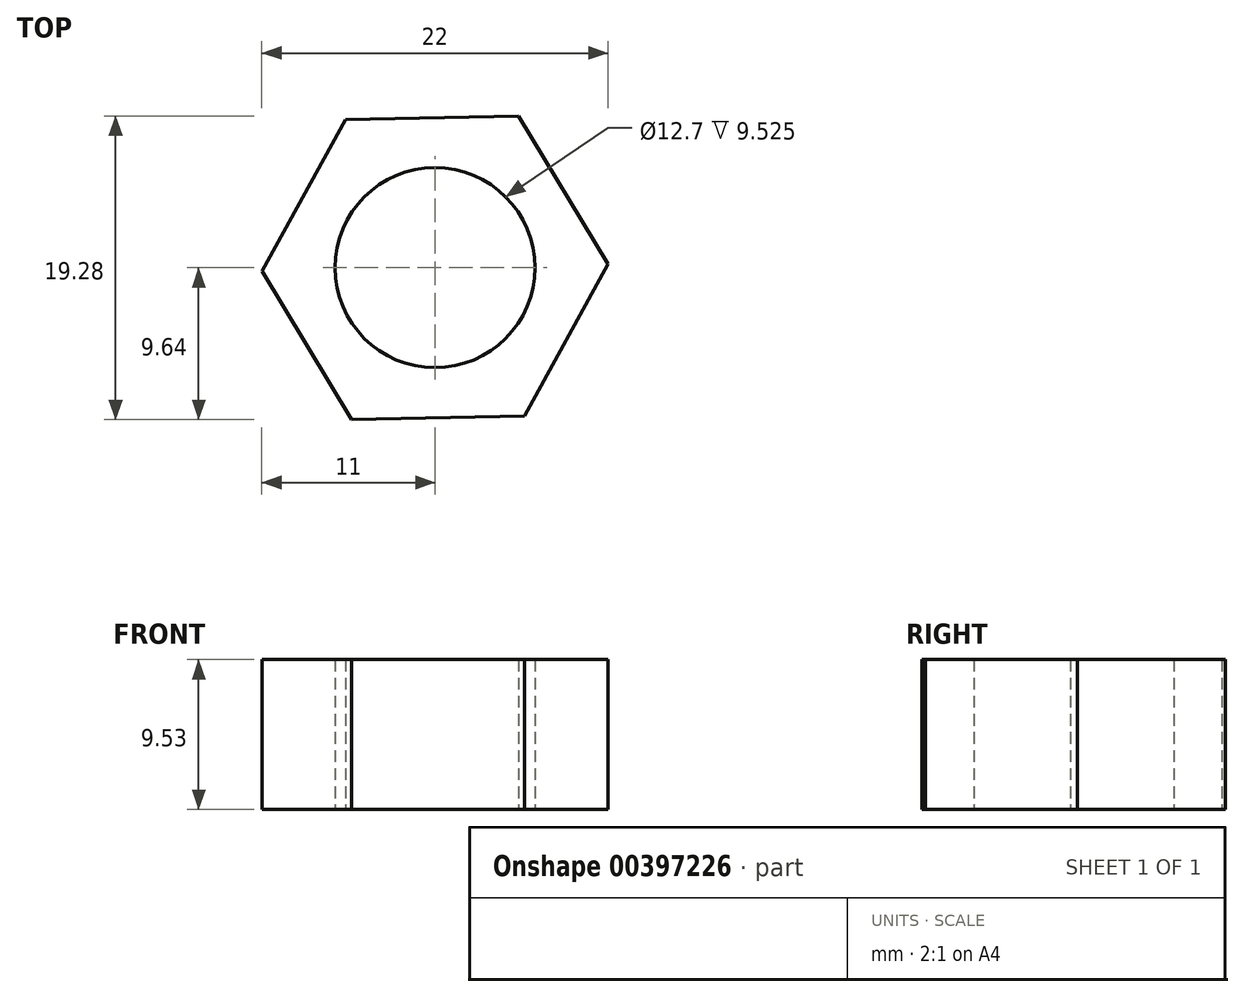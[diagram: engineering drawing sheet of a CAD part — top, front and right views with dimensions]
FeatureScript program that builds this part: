
annotation { "Feature Type Name" : "Feature", "Feature Type Description" : "" }
export const myFeature = defineFeature(function(context is Context, id is Id, definition is map)
    precondition{}
    {
        {
            var Q0;
            Q0=qCreatedBy(makeId("Top.planeOp"),FACE);
            var sketch = newSketch(context, id + "F0", { "sketchPlane" : qUnion([Q0])});
            skCircle(sketch, "E0.cCircle", {"center": v(0, 0) * mm, "radius": 9.53 * mm, "construction": true});
            skLineSegment(sketch, "E0.0", {"start": v(5.3, 9.64) * mm, "end": v(11, 0.22) * mm});
            skLineSegment(sketch, "E0.1", {"start": v(11, 0.22) * mm, "end": v(5.7, -9.41) * mm});
            skLineSegment(sketch, "E0.2", {"start": v(5.7, -9.41) * mm, "end": v(-5.3, -9.64) * mm});
            skLineSegment(sketch, "E0.3", {"start": v(-5.3, -9.64) * mm, "end": v(-11, -0.22) * mm});
            skLineSegment(sketch, "E0.4", {"start": v(-11, -0.22) * mm, "end": v(-5.7, 9.41) * mm});
            skLineSegment(sketch, "E0.5", {"start": v(-5.7, 9.41) * mm, "end": v(5.3, 9.64) * mm});
            skPoint(sketch, "E0.0.midPoint", {"position": v(8.15, 4.93) * mm});
            skCircle(sketch, "E1", {"center": v(0, 0) * mm, "radius": 6.35 * mm});
            skSolve(sketch);
        }
        {
            var Q0;
            Q0=qSketchRegion(id+"F0",true);
            extrude(context, id + "F1", {"entities" : qUnion([Q0]), "depth" : 9.52 * mm});
        }
    });
